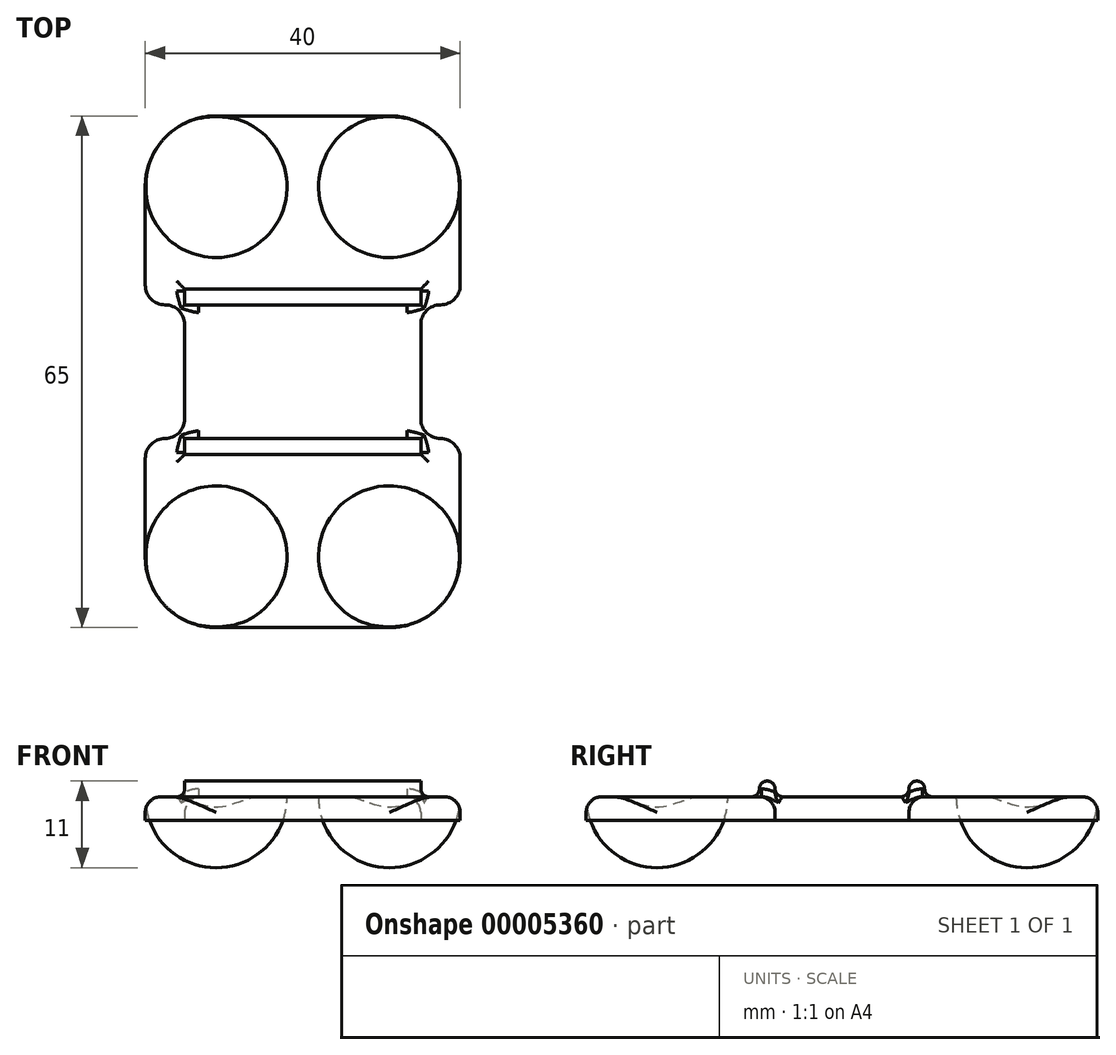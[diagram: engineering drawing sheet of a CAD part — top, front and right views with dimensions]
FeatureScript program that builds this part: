
annotation { "Feature Type Name" : "Feature", "Feature Type Description" : "" }
export const myFeature = defineFeature(function(context is Context, id is Id, definition is map)
    precondition{}
    {
        {
            var Q0;
            Q0=qCreatedBy(makeId("Top.planeOp"),FACE);
            var sketch = newSketch(context, id + "F0", { "sketchPlane" : qUnion([Q0])});
            skLineSegment(sketch, "E0.rect.bottom", {"start": v(20, 32.5) * mm, "end": v(-20, 32.5) * mm});
            skLineSegment(sketch, "E0.rect.top", {"start": v(20, -32.5) * mm, "end": v(-20, -32.5) * mm});
            skLineSegment(sketch, "E0.rect.left", {"start": v(20, 32.5) * mm, "end": v(20, -32.5) * mm});
            skLineSegment(sketch, "E0.rect.right", {"start": v(-20, 32.5) * mm, "end": v(-20, -32.5) * mm});
            skPoint(sketch, "E0.rect.middle", {"position": v(0, 0) * mm});
            skLineSegment(sketch, "E1.bottom", {"start": v(-20, -8.5) * mm, "end": v(-15, -8.5) * mm});
            skLineSegment(sketch, "E1.top", {"start": v(-20, 8.5) * mm, "end": v(-15, 8.5) * mm});
            skLineSegment(sketch, "E1.left", {"start": v(-20, -8.5) * mm, "end": v(-20, 8.5) * mm});
            skLineSegment(sketch, "E1.right", {"start": v(-15, -8.5) * mm, "end": v(-15, 8.5) * mm});
            skLineSegment(sketch, "E2.MirrorCS", {"start": v(20, -8.5) * mm, "end": v(15, -8.5) * mm});
            skLineSegment(sketch, "E3.MirrorCS", {"start": v(20, 8.5) * mm, "end": v(15, 8.5) * mm});
            skLineSegment(sketch, "E4.MirrorCS", {"start": v(15, -8.5) * mm, "end": v(15, 8.5) * mm});
            skLineSegment(sketch, "E5.bottom", {"start": v(-15, 8.5) * mm, "end": v(15, 8.5) * mm});
            skLineSegment(sketch, "E5.top", {"start": v(-15, 10.5) * mm, "end": v(15, 10.5) * mm});
            skLineSegment(sketch, "E5.left", {"start": v(-15, 8.5) * mm, "end": v(-15, 10.5) * mm});
            skLineSegment(sketch, "E5.right", {"start": v(15, 8.5) * mm, "end": v(15, 10.5) * mm});
            skLineSegment(sketch, "E6.MirrorCS", {"start": v(-15, -10.5) * mm, "end": v(15, -10.5) * mm});
            skLineSegment(sketch, "E7.MirrorCS", {"start": v(15, -8.5) * mm, "end": v(15, -10.5) * mm});
            skLineSegment(sketch, "E8.MirrorCS", {"start": v(-15, -8.5) * mm, "end": v(15, -8.5) * mm});
            skLineSegment(sketch, "E9.MirrorCS", {"start": v(-15, -8.5) * mm, "end": v(-15, -10.5) * mm});
            skSolve(sketch);
        }
        {
            var Q0;
            Q0=makeQuery(id+"F0.imprint","IMPRINT",FACE,{"disambiguationData":[TD([[makeQuery(id+"F0.imprint","IMPRINT",EDGE,{"derivedFrom":sQuery(id+"F0.wireOp",EDGE,"E0.rect.bottom")}),1.0]])]});
            var Q1;
            Q1=makeQuery(id+"F0.imprint","IMPRINT",FACE,{"disambiguationData":[TD([[makeQuery(id+"F0.imprint","IMPRINT",EDGE,{"derivedFrom":sQuery(id+"F0.wireOp",EDGE,"bcf83515-ba27-4b76-bd59-bfaced73eee4.0")}),1.0]])]});
            var Q2;
            Q2=makeQuery(id+"F0.imprint","IMPRINT",FACE,{"disambiguationData":[TD([[makeQuery(id+"F0.imprint","IMPRINT",EDGE,{"derivedFrom":sQuery(id+"F0.wireOp",EDGE,"E5.bottom")}),1.0]])]});
            var Q3;
            Q3=makeQuery(id+"F0.imprint","IMPRINT",FACE,{"disambiguationData":[TD([[makeQuery(id+"F0.imprint","IMPRINT",EDGE,{"derivedFrom":sQuery(id+"F0.wireOp",EDGE,"E1.right")}),-1.0]])]});
            var Q4;
            Q4=makeQuery(id+"F0.imprint","IMPRINT",FACE,{"disambiguationData":[TD([[makeQuery(id+"F0.imprint","IMPRINT",EDGE,{"derivedFrom":sQuery(id+"F0.wireOp",EDGE,"E6.MirrorCS")}),1.0]])]});
            var Q5;
            {var subQ2=sQuery(id+"F0.wireOp",EDGE,"E0.rect.top");Q5=makeQuery(id+"F0.imprint","IMPRINT",FACE,{"disambiguationData":[TD([[makeQuery(id+"F0.imprint","IMPRINT",EDGE,{"derivedFrom":subQ2}),-1.0]])]});}
            extrude(context, id + "F1", {"entities" : qUnion([Q0, Q1, Q2, Q3, Q4, Q5]), "depth" : 3 * mm});
        }
        {
            var Q0;
            Q0=makeQuery(id+"F1.opExtrude","CAP_FACE",FACE,{"disambiguationData":[OSD([sQuery(id+"F0.wireOp",EDGE,"E0.rect.bottom"),sQuery(id+"F0.wireOp",EDGE,"E0.rect.top"),sQuery(id+"F0.wireOp",EDGE,"E0.rect.left"),sQuery(id+"F0.wireOp",EDGE,"E0.rect.right")])],"isStart":false});
            var sketch = newSketch(context, id + "F2", { "sketchPlane" : qUnion([Q0])});
            skCircle(sketch, "E10", {"center": v(-11, 23.5) * mm, "radius": 9 * mm});
            skLineSegment(sketch, "E11", {"start": v(-11, 32.5) * mm, "end": v(-11, 14.5) * mm});
            skCircle(sketch, "E12", {"center": v(11, 23.5) * mm, "radius": 9 * mm});
            skCircle(sketch, "E13", {"center": v(-11, -23.5) * mm, "radius": 9 * mm});
            skCircle(sketch, "E14", {"center": v(11, -23.5) * mm, "radius": 9 * mm});
            skLineSegment(sketch, "E15", {"start": v(-11, -14.5) * mm, "end": v(-11, -32.5) * mm});
            skLineSegment(sketch, "E16", {"start": v(11, -14.5) * mm, "end": v(11, -32.5) * mm});
            skLineSegment(sketch, "E17", {"start": v(11, 14.5) * mm, "end": v(11, 32.5) * mm});
            skSolve(sketch);
        }
        {
            var Q0;
            {var subQ0=sQuery(id+"F2.wireOp",EDGE,"E11");Q0=makeQuery(id+"F2.imprint","IMPRINT",FACE,{"disambiguationData":[TD([[makeQuery(id+"F2.imprint","IMPRINT",EDGE,{"derivedFrom":subQ0}),-1.0]])]});}
            var Q1;
            Q1=sQuery(id+"F2.wireOp",EDGE,"E11");
            revolve(context, id + "F3", {"operationType" : NewBodyOperationType.ADD, "entities" : qUnion([Q0]), "axis" : qUnion([Q1]), "revolveType" : RevolveType.ONE_DIRECTION, "oppositeDirection" : true, "angle" : 180 * degree});
        }
        {
            var Q0;
            {var subQ0=sQuery(id+"F2.wireOp",EDGE,"E17");Q0=makeQuery(id+"F2.imprint","IMPRINT",FACE,{"disambiguationData":[TD([[makeQuery(id+"F2.imprint","IMPRINT",EDGE,{"derivedFrom":subQ0}),1.0]])]});}
            var Q1;
            Q1=sQuery(id+"F2.wireOp",EDGE,"E17");
            revolve(context, id + "F4", {"operationType" : NewBodyOperationType.ADD, "entities" : qUnion([Q0]), "axis" : qUnion([Q1]), "revolveType" : RevolveType.ONE_DIRECTION, "angle" : 180 * degree});
        }
        {
            var Q0;
            {var subQ0=sQuery(id+"F2.wireOp",EDGE,"E15");Q0=makeQuery(id+"F2.imprint","IMPRINT",FACE,{"disambiguationData":[TD([[makeQuery(id+"F2.imprint","IMPRINT",EDGE,{"derivedFrom":subQ0}),-1.0]])]});}
            var Q1;
            Q1=sQuery(id+"F2.wireOp",EDGE,"E15");
            revolve(context, id + "F5", {"operationType" : NewBodyOperationType.ADD, "entities" : qUnion([Q0]), "axis" : qUnion([Q1]), "revolveType" : RevolveType.ONE_DIRECTION, "oppositeDirection" : true, "angle" : 180 * degree});
        }
        {
            var Q0;
            {var subQ0=sQuery(id+"F2.wireOp",EDGE,"E16");Q0=makeQuery(id+"F2.imprint","IMPRINT",FACE,{"disambiguationData":[TD([[makeQuery(id+"F2.imprint","IMPRINT",EDGE,{"derivedFrom":subQ0}),-1.0]])]});}
            var Q1;
            Q1=sQuery(id+"F2.wireOp",EDGE,"E16");
            revolve(context, id + "F6", {"operationType" : NewBodyOperationType.ADD, "entities" : qUnion([Q0]), "axis" : qUnion([Q1]), "revolveType" : RevolveType.ONE_DIRECTION, "oppositeDirection" : true, "angle" : 180 * degree});
        }
        {
            var Q0;
            {var subQ0=sQuery(id+"F2.wireOp",EDGE,"E14");var subQ1=sQuery(id+"F0.wireOp",EDGE,"E0.rect.top");var subQ2=makeQuery(id+"F1.opExtrude","CAP_EDGE",EDGE,{"disambiguationData":[OSD([subQ1])],"isStart":false});var subQ3=makeQuery(id+"F2.imprint","INTERSECT",VERTEX,{"derivedFrom":[subQ2,subQ0,sQuery(id+"F2.wireOp",EDGE,"E16")]});Q0=makeQuery(id+"F2.imprint","IMPRINT",FACE,{"disambiguationData":[TD([[makeQuery(id+"F2.imprint","IMPRINT",EDGE,{"disambiguationData":[TD([[subQ3,-1.0]])],"derivedFrom":subQ0}),-1.0]])]});}
            var Q1;
            {var subQ0=sQuery(id+"F2.wireOp",EDGE,"E13");var subQ1=sQuery(id+"F0.wireOp",EDGE,"E0.rect.top");var subQ2=makeQuery(id+"F1.opExtrude","CAP_EDGE",EDGE,{"disambiguationData":[OSD([subQ1])],"isStart":false});var subQ3=makeQuery(id+"F2.imprint","INTERSECT",VERTEX,{"derivedFrom":[subQ2,subQ0,sQuery(id+"F2.wireOp",EDGE,"E15")]});Q1=makeQuery(id+"F2.imprint","IMPRINT",FACE,{"disambiguationData":[TD([[makeQuery(id+"F2.imprint","IMPRINT",EDGE,{"disambiguationData":[TD([[subQ3,1.0]])],"derivedFrom":subQ0}),-1.0]])]});}
            var Q2;
            {var subQ0=sQuery(id+"F2.wireOp",EDGE,"E10");var subQ1=sQuery(id+"F0.wireOp",EDGE,"E0.rect.bottom");var subQ2=makeQuery(id+"F1.opExtrude","CAP_EDGE",EDGE,{"disambiguationData":[OSD([subQ1])],"isStart":false});var subQ3=makeQuery(id+"F2.imprint","INTERSECT",VERTEX,{"derivedFrom":[subQ2,sQuery(id+"F2.wireOp",EDGE,"E11"),subQ0]});Q2=makeQuery(id+"F2.imprint","IMPRINT",FACE,{"disambiguationData":[TD([[makeQuery(id+"F2.imprint","IMPRINT",EDGE,{"disambiguationData":[TD([[subQ3,-1.0]])],"derivedFrom":subQ0}),-1.0]])]});}
            var Q3;
            {var subQ0=sQuery(id+"F2.wireOp",EDGE,"E12");var subQ1=sQuery(id+"F0.wireOp",EDGE,"E0.rect.bottom");var subQ2=makeQuery(id+"F1.opExtrude","CAP_EDGE",EDGE,{"disambiguationData":[OSD([subQ1])],"isStart":false});var subQ3=makeQuery(id+"F2.imprint","INTERSECT",VERTEX,{"derivedFrom":[subQ2,subQ0,sQuery(id+"F2.wireOp",EDGE,"E17")]});Q3=makeQuery(id+"F2.imprint","IMPRINT",FACE,{"disambiguationData":[TD([[makeQuery(id+"F2.imprint","IMPRINT",EDGE,{"disambiguationData":[TD([[subQ3,1.0]])],"derivedFrom":subQ0}),-1.0]])]});}
            extrude(context, id + "F7", {"entities" : qUnion([Q0, Q1, Q2, Q3]), "operationType" : NewBodyOperationType.REMOVE, "oppositeDirection" : true, "depth" : 5 * mm});
        }
        {
            var Q0;
            Q0=makeQuery(id+"F1.opExtrude","SWEPT_EDGE",EDGE,{"disambiguationData":[OSD([sQuery(id+"F0.wireOp",EDGE,"E0.rect.left"),sQuery(id+"F0.wireOp",EDGE,"E2.MirrorCS")])]});
            var Q1;
            Q1=makeQuery(id+"F1.opExtrude","SWEPT_EDGE",EDGE,{"disambiguationData":[OSD([sQuery(id+"F0.wireOp",EDGE,"E0.rect.left"),sQuery(id+"F0.wireOp",EDGE,"E3.MirrorCS")])]});
            var Q2;
            Q2=makeQuery(id+"F1.opExtrude","SWEPT_EDGE",EDGE,{"disambiguationData":[OSD([sQuery(id+"F0.wireOp",EDGE,"E3.MirrorCS"),sQuery(id+"F0.wireOp",EDGE,"E4.MirrorCS")])]});
            var Q3;
            Q3=makeQuery(id+"F1.opExtrude","SWEPT_EDGE",EDGE,{"disambiguationData":[OSD([sQuery(id+"F0.wireOp",EDGE,"E2.MirrorCS"),sQuery(id+"F0.wireOp",EDGE,"E4.MirrorCS")])]});
            var Q4;
            Q4=makeQuery(id+"F1.opExtrude","SWEPT_EDGE",EDGE,{"disambiguationData":[OSD([sQuery(id+"F0.wireOp",EDGE,"E0.rect.right"),sQuery(id+"F0.wireOp",EDGE,"E1.top"),sQuery(id+"F0.wireOp",EDGE,"E1.left")])]});
            var Q5;
            Q5=makeQuery(id+"F1.opExtrude","SWEPT_EDGE",EDGE,{"disambiguationData":[OSD([sQuery(id+"F0.wireOp",EDGE,"E1.top"),sQuery(id+"F0.wireOp",EDGE,"E1.right")])]});
            var Q6;
            Q6=makeQuery(id+"F1.opExtrude","SWEPT_EDGE",EDGE,{"disambiguationData":[OSD([sQuery(id+"F0.wireOp",EDGE,"E0.rect.right"),sQuery(id+"F0.wireOp",EDGE,"E1.bottom"),sQuery(id+"F0.wireOp",EDGE,"E1.left")])]});
            var Q7;
            Q7=makeQuery(id+"F1.opExtrude","SWEPT_EDGE",EDGE,{"disambiguationData":[OSD([sQuery(id+"F0.wireOp",EDGE,"E1.bottom"),sQuery(id+"F0.wireOp",EDGE,"E1.right")])]});
            fillet(context, id + "F8", {"entities" : qUnion([Q0, Q1, Q2, Q3, Q4, Q5, Q6, Q7]), "radius" : 2.5 * mm, "tangentPropagation" : true, "allowEdgeOverflow" : false});
        }
        {
            var Q0;
            {var subQ0=sQuery(id+"F0.wireOp",EDGE,"E1.top");var subQ1=sQuery(id+"F0.wireOp",EDGE,"E0.rect.right");var subQ2=sQuery(id+"F0.wireOp",EDGE,"E0.rect.bottom");var subQ3=makeQuery(id+"F0.imprint","IMPRINT",EDGE,{"disambiguationData":[TD([[makeQuery(id+"F0.imprint","INTERSECT",VERTEX,{"derivedFrom":[subQ2,subQ1]}),-1.0]])],"derivedFrom":subQ1});Q0=makeQuery(id+"F3.boolean.opBoolean","SPLIT",EDGE,{"disambiguationData":[TD([makeQuery(id+"F1.opExtrude","SWEPT_FACE",FACE,{"disambiguationData":[OSD([subQ0])]})])],"derivedFrom":makeQuery(id+"F1.opExtrude","CAP_EDGE",EDGE,{"disambiguationData":[OSD([subQ1]),TDD([subQ3])],"isStart":false})});}
            var Q1;
            Q1=makeQuery(id+"F1.opExtrude","CAP_EDGE",EDGE,{"disambiguationData":[OSD([sQuery(id+"F0.wireOp",EDGE,"E4.MirrorCS")])],"isStart":false});
            fillet(context, id + "F9", {"entities" : qUnion([Q0, Q1]), "radius" : 2 * mm, "tangentPropagation" : true, "allowEdgeOverflow" : false});
        }
        {
            var Q0;
            Q0=makeQuery(id+"F0.imprint","IMPRINT",FACE,{"disambiguationData":[TD([[makeQuery(id+"F0.imprint","IMPRINT",EDGE,{"derivedFrom":sQuery(id+"F0.wireOp",EDGE,"E6.MirrorCS")}),1.0]])]});
            var Q1;
            Q1=makeQuery(id+"F0.imprint","IMPRINT",FACE,{"disambiguationData":[TD([[makeQuery(id+"F0.imprint","IMPRINT",EDGE,{"derivedFrom":sQuery(id+"F0.wireOp",EDGE,"E5.bottom")}),1.0]])]});
            extrude(context, id + "F10", {"entities" : qUnion([Q0, Q1]), "operationType" : NewBodyOperationType.ADD, "depth" : 5 * mm});
        }
        {
            var Q0;
            Q0=makeQuery(id+"F10.opExtrude","CAP_EDGE",EDGE,{"disambiguationData":[OSD([sQuery(id+"F0.wireOp",EDGE,"E6.MirrorCS")])],"isStart":false});
            var Q1;
            Q1=makeQuery(id+"F10.opExtrude","CAP_EDGE",EDGE,{"disambiguationData":[OSD([sQuery(id+"F0.wireOp",EDGE,"E8.MirrorCS")])],"isStart":false});
            var Q2;
            Q2=makeQuery(id+"F10.opExtrude","CAP_EDGE",EDGE,{"disambiguationData":[OSD([sQuery(id+"F0.wireOp",EDGE,"E5.bottom")])],"isStart":false});
            var Q3;
            Q3=makeQuery(id+"F10.opExtrude","CAP_EDGE",EDGE,{"disambiguationData":[OSD([sQuery(id+"F0.wireOp",EDGE,"E5.top")])],"isStart":false});
            var Q4;
            {var subQ0=sQuery(id+"F0.wireOp",EDGE,"E1.top");var subQ1=makeQuery(id+"F1.opExtrude","SWEPT_FACE",FACE,{"disambiguationData":[OSD([subQ0])]});var subQ2=makeQuery(id+"F5.opRevolve","SWEPT_FACE",FACE,{"disambiguationData":[OSD([sQuery(id+"F2.wireOp",EDGE,"E13")])]});var subQ3=sQuery(id+"F0.wireOp",EDGE,"E1.bottom");var subQ4=makeQuery(id+"F1.opExtrude","SWEPT_FACE",FACE,{"disambiguationData":[OSD([subQ3])]});var subQ5=sQuery(id+"F0.wireOp",EDGE,"E0.rect.right");var subQ6=sQuery(id+"F0.wireOp",EDGE,"E0.rect.top");var subQ8=makeQuery(id+"F1.opExtrude","SWEPT_FACE",FACE,{"disambiguationData":[OSD([subQ5]),TDD([makeQuery(id+"F0.imprint","IMPRINT",EDGE,{"disambiguationData":[TD([[makeQuery(id+"F0.imprint","INTERSECT",VERTEX,{"derivedFrom":[subQ6,subQ5]}),1.0]])],"derivedFrom":subQ5})])]});var subQ9=sQuery(id+"F0.wireOp",EDGE,"E0.rect.bottom");var subQ10=makeQuery(id+"F1.opExtrude","SWEPT_FACE",FACE,{"disambiguationData":[OSD([subQ5]),TDD([makeQuery(id+"F0.imprint","IMPRINT",EDGE,{"disambiguationData":[TD([[makeQuery(id+"F0.imprint","INTERSECT",VERTEX,{"derivedFrom":[subQ9,subQ5]}),-1.0]])],"derivedFrom":subQ5})])]});var subQ11=sQuery(id+"F0.wireOp",EDGE,"E0.rect.left");var subQ12=sQuery(id+"F0.wireOp",EDGE,"E2.MirrorCS");var subQ13=makeQuery(id+"F1.opExtrude","SWEPT_FACE",FACE,{"disambiguationData":[OSD([subQ11]),TDD([makeQuery(id+"F0.imprint","IMPRINT",EDGE,{"disambiguationData":[TD([[makeQuery(id+"F0.imprint","INTERSECT",VERTEX,{"derivedFrom":[subQ6,subQ11]}),1.0]])],"derivedFrom":subQ11})])]});var subQ14=makeQuery(id+"F1.opExtrude","SWEPT_FACE",FACE,{"disambiguationData":[OSD([subQ9])]});var subQ15=sQuery(id+"F0.wireOp",EDGE,"E4.MirrorCS");var subQ16=sQuery(id+"F0.wireOp",EDGE,"E3.MirrorCS");var subQ17=sQuery(id+"F0.wireOp",EDGE,"E1.right");var subQ18=makeQuery(id+"F1.opExtrude","CAP_FACE",FACE,{"disambiguationData":[OSD([subQ9,subQ6,subQ11,subQ5,subQ3,subQ0,subQ17,subQ12,subQ16,subQ15])],"isStart":false});var subQ19=makeQuery(id+"F1.opExtrude","SWEPT_FACE",FACE,{"disambiguationData":[OSD([subQ15])]});var subQ20=makeQuery(id+"F1.opExtrude","SWEPT_FACE",FACE,{"disambiguationData":[OSD([subQ17])]});var subQ21=makeQuery(id+"F1.opExtrude","SWEPT_FACE",FACE,{"disambiguationData":[OSD([subQ6])]});var subQ22=makeQuery(id+"F1.opExtrude","SWEPT_FACE",FACE,{"disambiguationData":[OSD([subQ11]),TDD([makeQuery(id+"F0.imprint","IMPRINT",EDGE,{"disambiguationData":[TD([[makeQuery(id+"F0.imprint","INTERSECT",VERTEX,{"derivedFrom":[subQ9,subQ11]}),-1.0]])],"derivedFrom":subQ11})])]});var subQ23=makeQuery(id+"F4.opRevolve","SWEPT_FACE",FACE,{"disambiguationData":[OSD([sQuery(id+"F2.wireOp",EDGE,"E12")])]});var subQ24=makeQuery(id+"F1.opExtrude","SWEPT_FACE",FACE,{"disambiguationData":[OSD([subQ12])]});var subQ25=makeQuery(id+"F1.opExtrude","SWEPT_FACE",FACE,{"disambiguationData":[OSD([subQ16])]});var subQ26=makeQuery(id+"F3.opRevolve","SWEPT_FACE",FACE,{"disambiguationData":[OSD([sQuery(id+"F2.wireOp",EDGE,"E10")])]});Q4=makeQuery(id+"F10.boolean.opBoolean","INTERSECT",EDGE,{"derivedFrom":[makeQuery(id+"F6.boolean.opBoolean","SPLIT",FACE,{"disambiguationData":[TD([subQ14,subQ18,subQ21,subQ22,subQ13,subQ10,subQ8,subQ4,subQ1,subQ20,subQ24,subQ25,subQ19,subQ26,subQ23,subQ2,makeQuery(id+"F6.opRevolve","SWEPT_FACE",FACE,{"disambiguationData":[OSD([sQuery(id+"F2.wireOp",EDGE,"E14")])]})])],"derivedFrom":makeQuery(id+"F5.boolean.opBoolean","SPLIT",FACE,{"disambiguationData":[TD([subQ14,subQ18,subQ21,subQ22,subQ13,subQ10,subQ8,subQ4,subQ1,subQ20,subQ24,subQ25,subQ19,subQ26,subQ23,subQ2])],"derivedFrom":makeQuery(id+"F4.boolean.opBoolean","SPLIT",FACE,{"disambiguationData":[TD([subQ14,subQ18,subQ21,subQ22,subQ13,subQ10,subQ8,subQ4,subQ1,subQ20,subQ24,subQ25,subQ19,subQ26,subQ23])],"derivedFrom":makeQuery(id+"F3.boolean.opBoolean","SPLIT",FACE,{"disambiguationData":[TD([subQ14,subQ18,subQ21,subQ22,subQ13,subQ10,subQ8,subQ4,subQ1,subQ20,subQ24,subQ25,subQ19,subQ26])],"derivedFrom":subQ18})})})}),makeQuery(id+"F10.opExtrude","SWEPT_FACE",FACE,{"disambiguationData":[OSD([sQuery(id+"F0.wireOp",EDGE,"E8.MirrorCS")])]})]});}
            var Q5;
            {var subQ0=sQuery(id+"F0.wireOp",EDGE,"E1.top");var subQ1=makeQuery(id+"F1.opExtrude","SWEPT_FACE",FACE,{"disambiguationData":[OSD([subQ0])]});var subQ2=makeQuery(id+"F5.opRevolve","SWEPT_FACE",FACE,{"disambiguationData":[OSD([sQuery(id+"F2.wireOp",EDGE,"E13")])]});var subQ3=sQuery(id+"F0.wireOp",EDGE,"E1.bottom");var subQ4=makeQuery(id+"F1.opExtrude","SWEPT_FACE",FACE,{"disambiguationData":[OSD([subQ3])]});var subQ5=sQuery(id+"F0.wireOp",EDGE,"E0.rect.right");var subQ6=sQuery(id+"F0.wireOp",EDGE,"E0.rect.top");var subQ8=makeQuery(id+"F1.opExtrude","SWEPT_FACE",FACE,{"disambiguationData":[OSD([subQ5]),TDD([makeQuery(id+"F0.imprint","IMPRINT",EDGE,{"disambiguationData":[TD([[makeQuery(id+"F0.imprint","INTERSECT",VERTEX,{"derivedFrom":[subQ6,subQ5]}),1.0]])],"derivedFrom":subQ5})])]});var subQ9=sQuery(id+"F0.wireOp",EDGE,"E0.rect.bottom");var subQ10=makeQuery(id+"F1.opExtrude","SWEPT_FACE",FACE,{"disambiguationData":[OSD([subQ5]),TDD([makeQuery(id+"F0.imprint","IMPRINT",EDGE,{"disambiguationData":[TD([[makeQuery(id+"F0.imprint","INTERSECT",VERTEX,{"derivedFrom":[subQ9,subQ5]}),-1.0]])],"derivedFrom":subQ5})])]});var subQ11=sQuery(id+"F0.wireOp",EDGE,"E0.rect.left");var subQ12=sQuery(id+"F0.wireOp",EDGE,"E2.MirrorCS");var subQ13=makeQuery(id+"F1.opExtrude","SWEPT_FACE",FACE,{"disambiguationData":[OSD([subQ11]),TDD([makeQuery(id+"F0.imprint","IMPRINT",EDGE,{"disambiguationData":[TD([[makeQuery(id+"F0.imprint","INTERSECT",VERTEX,{"derivedFrom":[subQ6,subQ11]}),1.0]])],"derivedFrom":subQ11})])]});var subQ14=makeQuery(id+"F1.opExtrude","SWEPT_FACE",FACE,{"disambiguationData":[OSD([subQ9])]});var subQ15=sQuery(id+"F0.wireOp",EDGE,"E4.MirrorCS");var subQ16=sQuery(id+"F0.wireOp",EDGE,"E3.MirrorCS");var subQ17=sQuery(id+"F0.wireOp",EDGE,"E1.right");var subQ18=makeQuery(id+"F1.opExtrude","CAP_FACE",FACE,{"disambiguationData":[OSD([subQ9,subQ6,subQ11,subQ5,subQ3,subQ0,subQ17,subQ12,subQ16,subQ15])],"isStart":false});var subQ19=makeQuery(id+"F1.opExtrude","SWEPT_FACE",FACE,{"disambiguationData":[OSD([subQ15])]});var subQ20=makeQuery(id+"F1.opExtrude","SWEPT_FACE",FACE,{"disambiguationData":[OSD([subQ17])]});var subQ21=makeQuery(id+"F1.opExtrude","SWEPT_FACE",FACE,{"disambiguationData":[OSD([subQ6])]});var subQ22=makeQuery(id+"F1.opExtrude","SWEPT_FACE",FACE,{"disambiguationData":[OSD([subQ11]),TDD([makeQuery(id+"F0.imprint","IMPRINT",EDGE,{"disambiguationData":[TD([[makeQuery(id+"F0.imprint","INTERSECT",VERTEX,{"derivedFrom":[subQ9,subQ11]}),-1.0]])],"derivedFrom":subQ11})])]});var subQ23=makeQuery(id+"F4.opRevolve","SWEPT_FACE",FACE,{"disambiguationData":[OSD([sQuery(id+"F2.wireOp",EDGE,"E12")])]});var subQ24=makeQuery(id+"F1.opExtrude","SWEPT_FACE",FACE,{"disambiguationData":[OSD([subQ12])]});var subQ25=makeQuery(id+"F1.opExtrude","SWEPT_FACE",FACE,{"disambiguationData":[OSD([subQ16])]});var subQ26=makeQuery(id+"F3.opRevolve","SWEPT_FACE",FACE,{"disambiguationData":[OSD([sQuery(id+"F2.wireOp",EDGE,"E10")])]});Q5=makeQuery(id+"F10.boolean.opBoolean","INTERSECT",EDGE,{"derivedFrom":[makeQuery(id+"F6.boolean.opBoolean","SPLIT",FACE,{"disambiguationData":[TD([subQ14,subQ18,subQ21,subQ22,subQ13,subQ10,subQ8,subQ4,subQ1,subQ20,subQ24,subQ25,subQ19,subQ26,subQ23,subQ2,makeQuery(id+"F6.opRevolve","SWEPT_FACE",FACE,{"disambiguationData":[OSD([sQuery(id+"F2.wireOp",EDGE,"E14")])]})])],"derivedFrom":makeQuery(id+"F5.boolean.opBoolean","SPLIT",FACE,{"disambiguationData":[TD([subQ14,subQ18,subQ21,subQ22,subQ13,subQ10,subQ8,subQ4,subQ1,subQ20,subQ24,subQ25,subQ19,subQ26,subQ23,subQ2])],"derivedFrom":makeQuery(id+"F4.boolean.opBoolean","SPLIT",FACE,{"disambiguationData":[TD([subQ14,subQ18,subQ21,subQ22,subQ13,subQ10,subQ8,subQ4,subQ1,subQ20,subQ24,subQ25,subQ19,subQ26,subQ23])],"derivedFrom":makeQuery(id+"F3.boolean.opBoolean","SPLIT",FACE,{"disambiguationData":[TD([subQ14,subQ18,subQ21,subQ22,subQ13,subQ10,subQ8,subQ4,subQ1,subQ20,subQ24,subQ25,subQ19,subQ26])],"derivedFrom":subQ18})})})}),makeQuery(id+"F10.opExtrude","SWEPT_FACE",FACE,{"disambiguationData":[OSD([sQuery(id+"F0.wireOp",EDGE,"E6.MirrorCS")])]})]});}
            var Q6;
            {var subQ0=sQuery(id+"F0.wireOp",EDGE,"E1.top");var subQ1=makeQuery(id+"F1.opExtrude","SWEPT_FACE",FACE,{"disambiguationData":[OSD([subQ0])]});var subQ2=makeQuery(id+"F5.opRevolve","SWEPT_FACE",FACE,{"disambiguationData":[OSD([sQuery(id+"F2.wireOp",EDGE,"E13")])]});var subQ3=sQuery(id+"F0.wireOp",EDGE,"E1.bottom");var subQ4=makeQuery(id+"F1.opExtrude","SWEPT_FACE",FACE,{"disambiguationData":[OSD([subQ3])]});var subQ5=sQuery(id+"F0.wireOp",EDGE,"E0.rect.right");var subQ6=sQuery(id+"F0.wireOp",EDGE,"E0.rect.top");var subQ8=makeQuery(id+"F1.opExtrude","SWEPT_FACE",FACE,{"disambiguationData":[OSD([subQ5]),TDD([makeQuery(id+"F0.imprint","IMPRINT",EDGE,{"disambiguationData":[TD([[makeQuery(id+"F0.imprint","INTERSECT",VERTEX,{"derivedFrom":[subQ6,subQ5]}),1.0]])],"derivedFrom":subQ5})])]});var subQ9=sQuery(id+"F0.wireOp",EDGE,"E0.rect.bottom");var subQ10=makeQuery(id+"F1.opExtrude","SWEPT_FACE",FACE,{"disambiguationData":[OSD([subQ5]),TDD([makeQuery(id+"F0.imprint","IMPRINT",EDGE,{"disambiguationData":[TD([[makeQuery(id+"F0.imprint","INTERSECT",VERTEX,{"derivedFrom":[subQ9,subQ5]}),-1.0]])],"derivedFrom":subQ5})])]});var subQ11=sQuery(id+"F0.wireOp",EDGE,"E0.rect.left");var subQ12=sQuery(id+"F0.wireOp",EDGE,"E2.MirrorCS");var subQ13=makeQuery(id+"F1.opExtrude","SWEPT_FACE",FACE,{"disambiguationData":[OSD([subQ11]),TDD([makeQuery(id+"F0.imprint","IMPRINT",EDGE,{"disambiguationData":[TD([[makeQuery(id+"F0.imprint","INTERSECT",VERTEX,{"derivedFrom":[subQ6,subQ11]}),1.0]])],"derivedFrom":subQ11})])]});var subQ14=makeQuery(id+"F1.opExtrude","SWEPT_FACE",FACE,{"disambiguationData":[OSD([subQ9])]});var subQ15=sQuery(id+"F0.wireOp",EDGE,"E4.MirrorCS");var subQ16=sQuery(id+"F0.wireOp",EDGE,"E3.MirrorCS");var subQ17=sQuery(id+"F0.wireOp",EDGE,"E1.right");var subQ18=makeQuery(id+"F1.opExtrude","CAP_FACE",FACE,{"disambiguationData":[OSD([subQ9,subQ6,subQ11,subQ5,subQ3,subQ0,subQ17,subQ12,subQ16,subQ15])],"isStart":false});var subQ19=makeQuery(id+"F1.opExtrude","SWEPT_FACE",FACE,{"disambiguationData":[OSD([subQ15])]});var subQ20=makeQuery(id+"F1.opExtrude","SWEPT_FACE",FACE,{"disambiguationData":[OSD([subQ17])]});var subQ21=makeQuery(id+"F1.opExtrude","SWEPT_FACE",FACE,{"disambiguationData":[OSD([subQ6])]});var subQ22=makeQuery(id+"F1.opExtrude","SWEPT_FACE",FACE,{"disambiguationData":[OSD([subQ11]),TDD([makeQuery(id+"F0.imprint","IMPRINT",EDGE,{"disambiguationData":[TD([[makeQuery(id+"F0.imprint","INTERSECT",VERTEX,{"derivedFrom":[subQ9,subQ11]}),-1.0]])],"derivedFrom":subQ11})])]});var subQ23=makeQuery(id+"F4.opRevolve","SWEPT_FACE",FACE,{"disambiguationData":[OSD([sQuery(id+"F2.wireOp",EDGE,"E12")])]});var subQ24=makeQuery(id+"F1.opExtrude","SWEPT_FACE",FACE,{"disambiguationData":[OSD([subQ12])]});var subQ25=makeQuery(id+"F1.opExtrude","SWEPT_FACE",FACE,{"disambiguationData":[OSD([subQ16])]});var subQ26=makeQuery(id+"F3.opRevolve","SWEPT_FACE",FACE,{"disambiguationData":[OSD([sQuery(id+"F2.wireOp",EDGE,"E10")])]});Q6=makeQuery(id+"F10.boolean.opBoolean","INTERSECT",EDGE,{"derivedFrom":[makeQuery(id+"F6.boolean.opBoolean","SPLIT",FACE,{"disambiguationData":[TD([subQ14,subQ18,subQ21,subQ22,subQ13,subQ10,subQ8,subQ4,subQ1,subQ20,subQ24,subQ25,subQ19,subQ26,subQ23,subQ2,makeQuery(id+"F6.opRevolve","SWEPT_FACE",FACE,{"disambiguationData":[OSD([sQuery(id+"F2.wireOp",EDGE,"E14")])]})])],"derivedFrom":makeQuery(id+"F5.boolean.opBoolean","SPLIT",FACE,{"disambiguationData":[TD([subQ14,subQ18,subQ21,subQ22,subQ13,subQ10,subQ8,subQ4,subQ1,subQ20,subQ24,subQ25,subQ19,subQ26,subQ23,subQ2])],"derivedFrom":makeQuery(id+"F4.boolean.opBoolean","SPLIT",FACE,{"disambiguationData":[TD([subQ14,subQ18,subQ21,subQ22,subQ13,subQ10,subQ8,subQ4,subQ1,subQ20,subQ24,subQ25,subQ19,subQ26,subQ23])],"derivedFrom":makeQuery(id+"F3.boolean.opBoolean","SPLIT",FACE,{"disambiguationData":[TD([subQ14,subQ18,subQ21,subQ22,subQ13,subQ10,subQ8,subQ4,subQ1,subQ20,subQ24,subQ25,subQ19,subQ26])],"derivedFrom":subQ18})})})}),makeQuery(id+"F10.opExtrude","SWEPT_FACE",FACE,{"disambiguationData":[OSD([sQuery(id+"F0.wireOp",EDGE,"E5.bottom")])]})]});}
            var Q7;
            {var subQ0=sQuery(id+"F0.wireOp",EDGE,"E1.top");var subQ1=makeQuery(id+"F1.opExtrude","SWEPT_FACE",FACE,{"disambiguationData":[OSD([subQ0])]});var subQ2=makeQuery(id+"F5.opRevolve","SWEPT_FACE",FACE,{"disambiguationData":[OSD([sQuery(id+"F2.wireOp",EDGE,"E13")])]});var subQ3=sQuery(id+"F0.wireOp",EDGE,"E1.bottom");var subQ4=makeQuery(id+"F1.opExtrude","SWEPT_FACE",FACE,{"disambiguationData":[OSD([subQ3])]});var subQ5=sQuery(id+"F0.wireOp",EDGE,"E0.rect.right");var subQ6=sQuery(id+"F0.wireOp",EDGE,"E0.rect.top");var subQ8=makeQuery(id+"F1.opExtrude","SWEPT_FACE",FACE,{"disambiguationData":[OSD([subQ5]),TDD([makeQuery(id+"F0.imprint","IMPRINT",EDGE,{"disambiguationData":[TD([[makeQuery(id+"F0.imprint","INTERSECT",VERTEX,{"derivedFrom":[subQ6,subQ5]}),1.0]])],"derivedFrom":subQ5})])]});var subQ9=sQuery(id+"F0.wireOp",EDGE,"E0.rect.bottom");var subQ10=makeQuery(id+"F1.opExtrude","SWEPT_FACE",FACE,{"disambiguationData":[OSD([subQ5]),TDD([makeQuery(id+"F0.imprint","IMPRINT",EDGE,{"disambiguationData":[TD([[makeQuery(id+"F0.imprint","INTERSECT",VERTEX,{"derivedFrom":[subQ9,subQ5]}),-1.0]])],"derivedFrom":subQ5})])]});var subQ11=sQuery(id+"F0.wireOp",EDGE,"E0.rect.left");var subQ12=sQuery(id+"F0.wireOp",EDGE,"E2.MirrorCS");var subQ13=makeQuery(id+"F1.opExtrude","SWEPT_FACE",FACE,{"disambiguationData":[OSD([subQ11]),TDD([makeQuery(id+"F0.imprint","IMPRINT",EDGE,{"disambiguationData":[TD([[makeQuery(id+"F0.imprint","INTERSECT",VERTEX,{"derivedFrom":[subQ6,subQ11]}),1.0]])],"derivedFrom":subQ11})])]});var subQ14=makeQuery(id+"F1.opExtrude","SWEPT_FACE",FACE,{"disambiguationData":[OSD([subQ9])]});var subQ15=sQuery(id+"F0.wireOp",EDGE,"E4.MirrorCS");var subQ16=sQuery(id+"F0.wireOp",EDGE,"E3.MirrorCS");var subQ17=sQuery(id+"F0.wireOp",EDGE,"E1.right");var subQ18=makeQuery(id+"F1.opExtrude","CAP_FACE",FACE,{"disambiguationData":[OSD([subQ9,subQ6,subQ11,subQ5,subQ3,subQ0,subQ17,subQ12,subQ16,subQ15])],"isStart":false});var subQ19=makeQuery(id+"F1.opExtrude","SWEPT_FACE",FACE,{"disambiguationData":[OSD([subQ15])]});var subQ20=makeQuery(id+"F1.opExtrude","SWEPT_FACE",FACE,{"disambiguationData":[OSD([subQ17])]});var subQ21=makeQuery(id+"F1.opExtrude","SWEPT_FACE",FACE,{"disambiguationData":[OSD([subQ6])]});var subQ22=makeQuery(id+"F1.opExtrude","SWEPT_FACE",FACE,{"disambiguationData":[OSD([subQ11]),TDD([makeQuery(id+"F0.imprint","IMPRINT",EDGE,{"disambiguationData":[TD([[makeQuery(id+"F0.imprint","INTERSECT",VERTEX,{"derivedFrom":[subQ9,subQ11]}),-1.0]])],"derivedFrom":subQ11})])]});var subQ23=makeQuery(id+"F4.opRevolve","SWEPT_FACE",FACE,{"disambiguationData":[OSD([sQuery(id+"F2.wireOp",EDGE,"E12")])]});var subQ24=makeQuery(id+"F1.opExtrude","SWEPT_FACE",FACE,{"disambiguationData":[OSD([subQ12])]});var subQ25=makeQuery(id+"F1.opExtrude","SWEPT_FACE",FACE,{"disambiguationData":[OSD([subQ16])]});var subQ26=makeQuery(id+"F3.opRevolve","SWEPT_FACE",FACE,{"disambiguationData":[OSD([sQuery(id+"F2.wireOp",EDGE,"E10")])]});Q7=makeQuery(id+"F10.boolean.opBoolean","INTERSECT",EDGE,{"derivedFrom":[makeQuery(id+"F6.boolean.opBoolean","SPLIT",FACE,{"disambiguationData":[TD([subQ14,subQ18,subQ21,subQ22,subQ13,subQ10,subQ8,subQ4,subQ1,subQ20,subQ24,subQ25,subQ19,subQ26,subQ23,subQ2,makeQuery(id+"F6.opRevolve","SWEPT_FACE",FACE,{"disambiguationData":[OSD([sQuery(id+"F2.wireOp",EDGE,"E14")])]})])],"derivedFrom":makeQuery(id+"F5.boolean.opBoolean","SPLIT",FACE,{"disambiguationData":[TD([subQ14,subQ18,subQ21,subQ22,subQ13,subQ10,subQ8,subQ4,subQ1,subQ20,subQ24,subQ25,subQ19,subQ26,subQ23,subQ2])],"derivedFrom":makeQuery(id+"F4.boolean.opBoolean","SPLIT",FACE,{"disambiguationData":[TD([subQ14,subQ18,subQ21,subQ22,subQ13,subQ10,subQ8,subQ4,subQ1,subQ20,subQ24,subQ25,subQ19,subQ26,subQ23])],"derivedFrom":makeQuery(id+"F3.boolean.opBoolean","SPLIT",FACE,{"disambiguationData":[TD([subQ14,subQ18,subQ21,subQ22,subQ13,subQ10,subQ8,subQ4,subQ1,subQ20,subQ24,subQ25,subQ19,subQ26])],"derivedFrom":subQ18})})})}),makeQuery(id+"F10.opExtrude","SWEPT_FACE",FACE,{"disambiguationData":[OSD([sQuery(id+"F0.wireOp",EDGE,"E5.top")])]})]});}
            var Q8;
            {var subQ0=sQuery(id+"F0.wireOp",EDGE,"E7.MirrorCS");Q8=makeQuery(id+"F10.boolean.opBoolean","INTERSECT",EDGE,{"derivedFrom":[makeQuery(id+"F9.opFillet","BLEND_FACE",FACE,{"disambiguationData":[OSD([sQuery(id+"F0.wireOp",EDGE,"E0.rect.bottom"),sQuery(id+"F0.wireOp",EDGE,"E0.rect.top"),sQuery(id+"F0.wireOp",EDGE,"E0.rect.left"),sQuery(id+"F0.wireOp",EDGE,"E0.rect.right"),sQuery(id+"F0.wireOp",EDGE,"E1.bottom"),sQuery(id+"F0.wireOp",EDGE,"E1.top"),sQuery(id+"F0.wireOp",EDGE,"E1.right"),sQuery(id+"F0.wireOp",EDGE,"E2.MirrorCS"),sQuery(id+"F0.wireOp",EDGE,"E3.MirrorCS"),sQuery(id+"F0.wireOp",EDGE,"E4.MirrorCS"),subQ0,sQuery(id+"F0.wireOp",EDGE,"E8.MirrorCS")])]}),makeQuery(id+"F10.opExtrude","SWEPT_FACE",FACE,{"disambiguationData":[OSD([subQ0])]})]});}
            var Q9;
            {var subQ0=sQuery(id+"F0.wireOp",EDGE,"E5.right");Q9=makeQuery(id+"F10.boolean.opBoolean","INTERSECT",EDGE,{"derivedFrom":[makeQuery(id+"F9.opFillet","BLEND_FACE",FACE,{"disambiguationData":[OSD([sQuery(id+"F0.wireOp",EDGE,"E0.rect.bottom"),sQuery(id+"F0.wireOp",EDGE,"E0.rect.top"),sQuery(id+"F0.wireOp",EDGE,"E0.rect.left"),sQuery(id+"F0.wireOp",EDGE,"E0.rect.right"),sQuery(id+"F0.wireOp",EDGE,"E1.bottom"),sQuery(id+"F0.wireOp",EDGE,"E1.top"),sQuery(id+"F0.wireOp",EDGE,"E1.right"),sQuery(id+"F0.wireOp",EDGE,"E2.MirrorCS"),sQuery(id+"F0.wireOp",EDGE,"E3.MirrorCS"),sQuery(id+"F0.wireOp",EDGE,"E4.MirrorCS"),sQuery(id+"F0.wireOp",EDGE,"E5.bottom"),subQ0])]}),makeQuery(id+"F10.opExtrude","SWEPT_FACE",FACE,{"disambiguationData":[OSD([subQ0])]})]});}
            var Q10;
            {var subQ0=sQuery(id+"F0.wireOp",EDGE,"E5.left");Q10=makeQuery(id+"F10.boolean.opBoolean","INTERSECT",EDGE,{"derivedFrom":[makeQuery(id+"F9.opFillet","BLEND_FACE",FACE,{"disambiguationData":[OSD([sQuery(id+"F0.wireOp",EDGE,"E0.rect.bottom"),sQuery(id+"F0.wireOp",EDGE,"E0.rect.top"),sQuery(id+"F0.wireOp",EDGE,"E0.rect.left"),sQuery(id+"F0.wireOp",EDGE,"E0.rect.right"),sQuery(id+"F0.wireOp",EDGE,"E1.bottom"),sQuery(id+"F0.wireOp",EDGE,"E1.top"),sQuery(id+"F0.wireOp",EDGE,"E1.right"),sQuery(id+"F0.wireOp",EDGE,"E2.MirrorCS"),sQuery(id+"F0.wireOp",EDGE,"E3.MirrorCS"),sQuery(id+"F0.wireOp",EDGE,"E4.MirrorCS"),sQuery(id+"F0.wireOp",EDGE,"E5.bottom"),subQ0])]}),makeQuery(id+"F10.opExtrude","SWEPT_FACE",FACE,{"disambiguationData":[OSD([subQ0])]})]});}
            var Q11;
            {var subQ0=sQuery(id+"F0.wireOp",EDGE,"E9.MirrorCS");Q11=makeQuery(id+"F10.boolean.opBoolean","INTERSECT",EDGE,{"derivedFrom":[makeQuery(id+"F9.opFillet","BLEND_FACE",FACE,{"disambiguationData":[OSD([sQuery(id+"F0.wireOp",EDGE,"E0.rect.bottom"),sQuery(id+"F0.wireOp",EDGE,"E0.rect.top"),sQuery(id+"F0.wireOp",EDGE,"E0.rect.left"),sQuery(id+"F0.wireOp",EDGE,"E0.rect.right"),sQuery(id+"F0.wireOp",EDGE,"E1.bottom"),sQuery(id+"F0.wireOp",EDGE,"E1.top"),sQuery(id+"F0.wireOp",EDGE,"E1.right"),sQuery(id+"F0.wireOp",EDGE,"E2.MirrorCS"),sQuery(id+"F0.wireOp",EDGE,"E3.MirrorCS"),sQuery(id+"F0.wireOp",EDGE,"E4.MirrorCS"),sQuery(id+"F0.wireOp",EDGE,"E8.MirrorCS"),subQ0])]}),makeQuery(id+"F10.opExtrude","SWEPT_FACE",FACE,{"disambiguationData":[OSD([subQ0])]})]});}
            fillet(context, id + "F11", {"entities" : qUnion([Q0, Q1, Q2, Q3, Q4, Q5, Q6, Q7, Q8, Q9, Q10, Q11]), "radius" : 1 * mm, "tangentPropagation" : true, "allowEdgeOverflow" : false});
        }
    });
